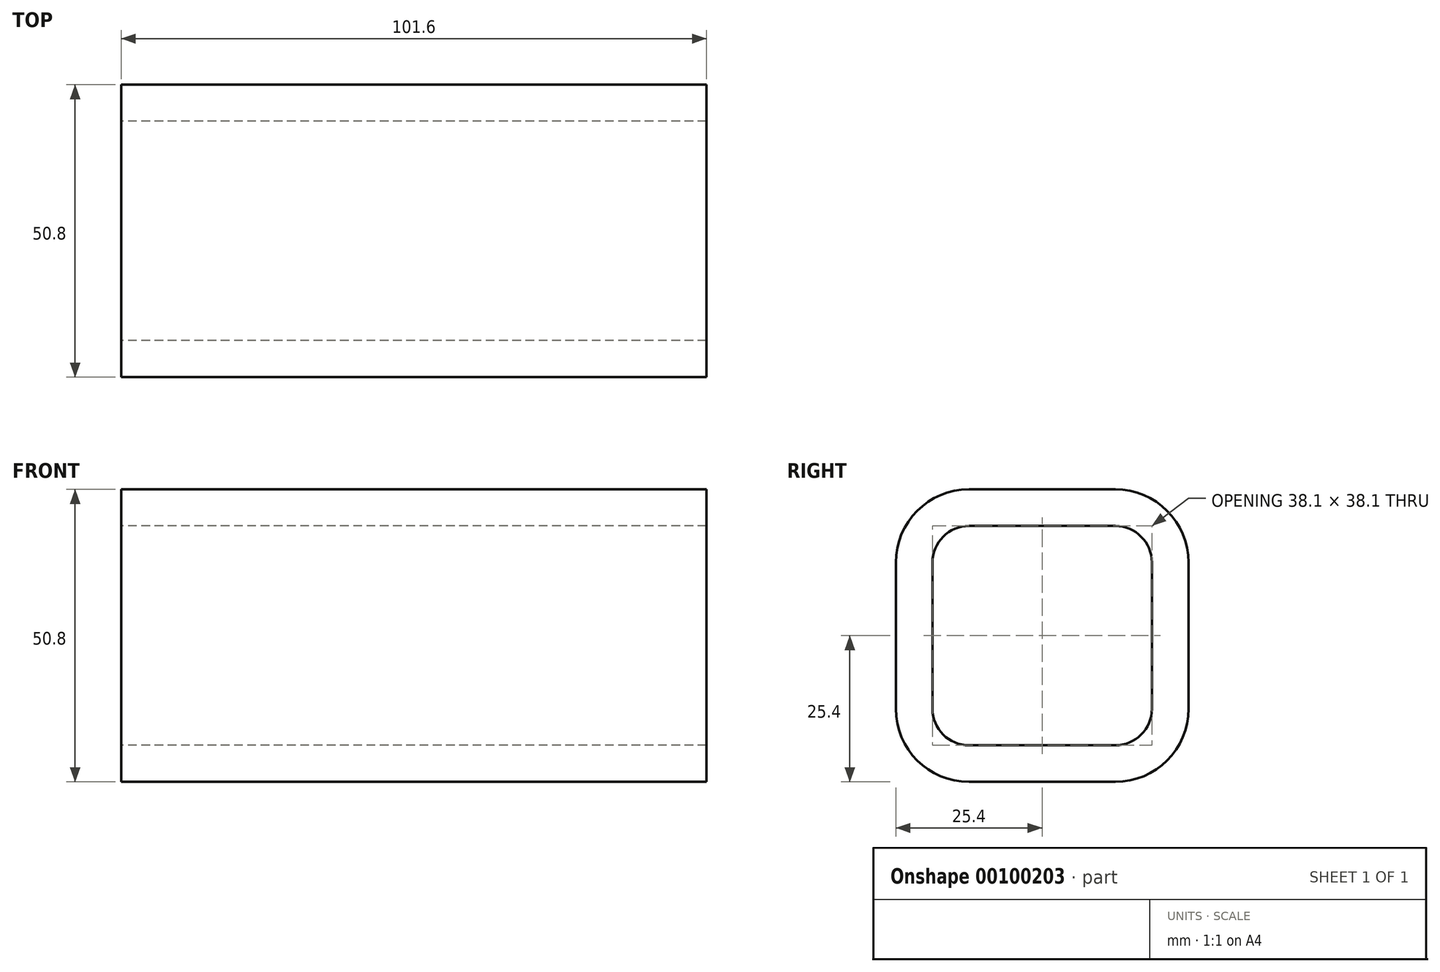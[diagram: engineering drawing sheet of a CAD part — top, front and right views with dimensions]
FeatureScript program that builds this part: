
annotation { "Feature Type Name" : "Feature", "Feature Type Description" : "" }
export const myFeature = defineFeature(function(context is Context, id is Id, definition is map)
    precondition{}
    {
        {
            var Q0;
            Q0=qCreatedBy(makeId("Right.planeOp"),FACE);
            var sketch = newSketch(context, id + "F0", { "sketchPlane" : qUnion([Q0])});
            skLineSegment(sketch, "E0.bottom", {"start": v(-12.7, -25.4) * mm, "end": v(12.7, -25.4) * mm});
            skLineSegment(sketch, "E0.top", {"start": v(-12.7, 25.4) * mm, "end": v(12.7, 25.4) * mm});
            skLineSegment(sketch, "E0.left", {"start": v(-25.4, -12.7) * mm, "end": v(-25.4, 12.7) * mm});
            skLineSegment(sketch, "E0.right", {"start": v(25.4, -12.7) * mm, "end": v(25.4, 12.7) * mm});
            skLineSegment(sketch, "E1", {"start": v(-25.4, 0) * mm, "end": v(25.4, 0) * mm, "construction": true});
            skLineSegment(sketch, "E2", {"start": v(0, 25.4) * mm, "end": v(0, -25.4) * mm, "construction": true});
            skPoint(sketch, "E3.visualSharp", {"position": v(-25.4, 25.4) * mm});
            skArc(sketch, "E3.filletArc", {"start": v(-12.7, 25.4) * mm, "mid": v(-21.68, 21.68) * mm, "end": v(-25.4, 12.7) * mm});
            skPoint(sketch, "E4.visualSharp", {"position": v(25.4, 25.4) * mm});
            skPoint(sketch, "E5.visualSharp", {"position": v(25.4, -25.4) * mm});
            skPoint(sketch, "E6.visualSharp", {"position": v(-25.4, -25.4) * mm});
            skArc(sketch, "E7.filletArc", {"start": v(25.4, 12.7) * mm, "mid": v(21.68, 21.68) * mm, "end": v(12.7, 25.4) * mm});
            skArc(sketch, "E8.filletArc", {"start": v(12.7, -25.4) * mm, "mid": v(21.68, -21.68) * mm, "end": v(25.4, -12.7) * mm});
            skArc(sketch, "E9.filletArc", {"start": v(-25.4, -12.7) * mm, "mid": v(-21.68, -21.68) * mm, "end": v(-12.7, -25.4) * mm});
            skLineSegment(sketch, "E10.0", {"start": v(-19.05, -12.7) * mm, "end": v(-19.05, 12.7) * mm});
            skArc(sketch, "E11.0", {"start": v(-12.7, 19.05) * mm, "mid": v(-17.2, 17.2) * mm, "end": v(-19.05, 12.7) * mm});
            skLineSegment(sketch, "E11.1", {"start": v(-12.7, 19.05) * mm, "end": v(12.7, 19.05) * mm});
            skArc(sketch, "E11.2", {"start": v(19.05, 12.7) * mm, "mid": v(17.2, 17.2) * mm, "end": v(12.7, 19.05) * mm});
            skArc(sketch, "E11.3", {"start": v(-19.05, -12.7) * mm, "mid": v(-17.2, -17.2) * mm, "end": v(-12.7, -19.05) * mm});
            skLineSegment(sketch, "E11.4", {"start": v(-12.7, -19.05) * mm, "end": v(12.7, -19.05) * mm});
            skArc(sketch, "E11.5", {"start": v(12.7, -19.05) * mm, "mid": v(17.2, -17.2) * mm, "end": v(19.05, -12.7) * mm});
            skLineSegment(sketch, "E11.6", {"start": v(19.05, -12.7) * mm, "end": v(19.05, 12.7) * mm});
            skSolve(sketch);
        }
        {
            var Q0;
            Q0 = qSketchRegion(id + "F0", true);
            extrude(context, id + "F1", {"entities" : qUnion([Q0]), "endBound" : BoundingType.SYMMETRIC, "depth" : 101.6 * mm});
        }
    });
